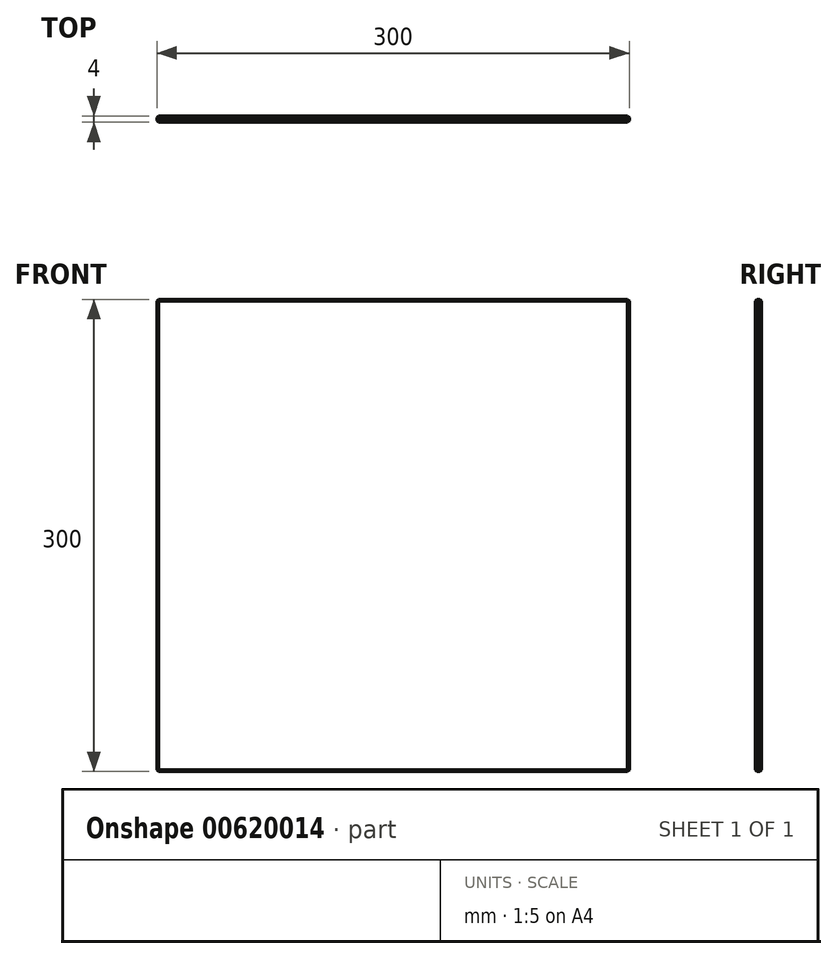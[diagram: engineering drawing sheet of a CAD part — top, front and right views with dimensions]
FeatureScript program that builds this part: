
annotation { "Feature Type Name" : "Feature", "Feature Type Description" : "" }
export const myFeature = defineFeature(function(context is Context, id is Id, definition is map)
    precondition{}
    {
        {
            var Q0;
            Q0=qCreatedBy(makeId("Front.planeOp"),FACE);
            var sketch = newSketch(context, id + "F0", { "sketchPlane" : qUnion([Q0])});
            skLineSegment(sketch, "E0.bottom", {"start": v(-262.15, 270.21) * mm, "end": v(37.85, 270.21) * mm});
            skLineSegment(sketch, "E0.top", {"start": v(-262.15, -29.79) * mm, "end": v(37.85, -29.79) * mm});
            skLineSegment(sketch, "E0.left", {"start": v(-262.15, 270.21) * mm, "end": v(-262.15, -29.79) * mm});
            skLineSegment(sketch, "E0.right", {"start": v(37.85, 270.21) * mm, "end": v(37.85, -29.79) * mm});
            skSolve(sketch);
        }
        {
            var Q0;
            Q0 = qSketchRegion(id + "F0", true);
            extrude(context, id + "F1", {"entities" : qUnion([Q0]), "depth" : 4 * mm, "offsetDistance" : 25 * mm});
        }
        {
            var Q0;
            Q0=makeQuery(id+"F1.opExtrude","SWEPT_EDGE",EDGE,{"disambiguationData":[OSD([sQuery(id+"F0.wireOp",EDGE,"E0.bottom"),sQuery(id+"F0.wireOp",EDGE,"E0.left")])]});
            var Q1;
            Q1=makeQuery(id+"F1.opExtrude","SWEPT_EDGE",EDGE,{"disambiguationData":[OSD([sQuery(id+"F0.wireOp",EDGE,"E0.bottom"),sQuery(id+"F0.wireOp",EDGE,"E0.right")])]});
            var Q2;
            Q2=makeQuery(id+"F1.opExtrude","SWEPT_EDGE",EDGE,{"disambiguationData":[OSD([sQuery(id+"F0.wireOp",EDGE,"E0.top"),sQuery(id+"F0.wireOp",EDGE,"E0.right")])]});
            var Q3;
            Q3=makeQuery(id+"F1.opExtrude","SWEPT_EDGE",EDGE,{"disambiguationData":[OSD([sQuery(id+"F0.wireOp",EDGE,"E0.top"),sQuery(id+"F0.wireOp",EDGE,"E0.left")])]});
            chamfer(context, id + "F2", {"entities" : qUnion([Q0, Q1, Q2, Q3]), "width" : 1 * mm, "tangentPropagation" : true});
        }
        {
            var Q0;
            Q0=makeQuery(id+"F1.opExtrude","CAP_EDGE",EDGE,{"disambiguationData":[OSD([sQuery(id+"F0.wireOp",EDGE,"E0.top")])],"isStart":false});
            var Q1;
            {var subQ0=sQuery(id+"F0.wireOp",EDGE,"E0.left");var subQ1=sQuery(id+"F0.wireOp",EDGE,"E0.top");Q1=makeQuery(id+"F2.opChamfer","BLEND_EDGE",EDGE,{"blendedFrom":[makeQuery(id+"F1.opExtrude","SWEPT_EDGE",EDGE,{"disambiguationData":[OSD([subQ1,subQ0])]}),makeQuery(id+"F1.opExtrude","CAP_FACE",FACE,{"disambiguationData":[OSD([sQuery(id+"F0.wireOp",EDGE,"E0.bottom"),subQ1,subQ0,sQuery(id+"F0.wireOp",EDGE,"E0.right")])],"isStart":false})],"blendedInto":[makeQuery(id+"F1.opExtrude","CAP_FACE",FACE,{"disambiguationData":[OSD([sQuery(id+"F0.wireOp",EDGE,"E0.bottom"),subQ1,subQ0,sQuery(id+"F0.wireOp",EDGE,"E0.right")])],"isStart":false})]});}
            var Q2;
            Q2=makeQuery(id+"F1.opExtrude","CAP_EDGE",EDGE,{"disambiguationData":[OSD([sQuery(id+"F0.wireOp",EDGE,"E0.left")])],"isStart":false});
            var Q3;
            {var subQ0=sQuery(id+"F0.wireOp",EDGE,"E0.right");var subQ1=sQuery(id+"F0.wireOp",EDGE,"E0.top");Q3=makeQuery(id+"F2.opChamfer","BLEND_EDGE",EDGE,{"blendedFrom":[makeQuery(id+"F1.opExtrude","SWEPT_EDGE",EDGE,{"disambiguationData":[OSD([subQ1,subQ0])]}),makeQuery(id+"F1.opExtrude","CAP_FACE",FACE,{"disambiguationData":[OSD([sQuery(id+"F0.wireOp",EDGE,"E0.bottom"),subQ1,sQuery(id+"F0.wireOp",EDGE,"E0.left"),subQ0])],"isStart":false})],"blendedInto":[makeQuery(id+"F1.opExtrude","CAP_FACE",FACE,{"disambiguationData":[OSD([sQuery(id+"F0.wireOp",EDGE,"E0.bottom"),subQ1,sQuery(id+"F0.wireOp",EDGE,"E0.left"),subQ0])],"isStart":false})]});}
            var Q4;
            Q4=makeQuery(id+"F1.opExtrude","CAP_EDGE",EDGE,{"disambiguationData":[OSD([sQuery(id+"F0.wireOp",EDGE,"E0.right")])],"isStart":false});
            var Q5;
            Q5=makeQuery(id+"F1.opExtrude","CAP_EDGE",EDGE,{"disambiguationData":[OSD([sQuery(id+"F0.wireOp",EDGE,"E0.right")])],"isStart":true});
            var Q6;
            {var subQ0=sQuery(id+"F0.wireOp",EDGE,"E0.right");var subQ1=sQuery(id+"F0.wireOp",EDGE,"E0.top");Q6=makeQuery(id+"F2.opChamfer","BLEND_EDGE",EDGE,{"blendedFrom":[makeQuery(id+"F1.opExtrude","SWEPT_EDGE",EDGE,{"disambiguationData":[OSD([subQ1,subQ0])]}),makeQuery(id+"F1.opExtrude","CAP_FACE",FACE,{"disambiguationData":[OSD([sQuery(id+"F0.wireOp",EDGE,"E0.bottom"),subQ1,sQuery(id+"F0.wireOp",EDGE,"E0.left"),subQ0])],"isStart":true})],"blendedInto":[makeQuery(id+"F1.opExtrude","CAP_FACE",FACE,{"disambiguationData":[OSD([sQuery(id+"F0.wireOp",EDGE,"E0.bottom"),subQ1,sQuery(id+"F0.wireOp",EDGE,"E0.left"),subQ0])],"isStart":true})]});}
            var Q7;
            Q7=makeQuery(id+"F1.opExtrude","CAP_EDGE",EDGE,{"disambiguationData":[OSD([sQuery(id+"F0.wireOp",EDGE,"E0.top")])],"isStart":true});
            var Q8;
            {var subQ0=sQuery(id+"F0.wireOp",EDGE,"E0.left");var subQ1=sQuery(id+"F0.wireOp",EDGE,"E0.top");Q8=makeQuery(id+"F2.opChamfer","BLEND_EDGE",EDGE,{"blendedFrom":[makeQuery(id+"F1.opExtrude","SWEPT_EDGE",EDGE,{"disambiguationData":[OSD([subQ1,subQ0])]}),makeQuery(id+"F1.opExtrude","CAP_FACE",FACE,{"disambiguationData":[OSD([sQuery(id+"F0.wireOp",EDGE,"E0.bottom"),subQ1,subQ0,sQuery(id+"F0.wireOp",EDGE,"E0.right")])],"isStart":true})],"blendedInto":[makeQuery(id+"F1.opExtrude","CAP_FACE",FACE,{"disambiguationData":[OSD([sQuery(id+"F0.wireOp",EDGE,"E0.bottom"),subQ1,subQ0,sQuery(id+"F0.wireOp",EDGE,"E0.right")])],"isStart":true})]});}
            var Q9;
            Q9=makeQuery(id+"F1.opExtrude","CAP_EDGE",EDGE,{"disambiguationData":[OSD([sQuery(id+"F0.wireOp",EDGE,"E0.left")])],"isStart":true});
            var Q10;
            {var subQ0=sQuery(id+"F0.wireOp",EDGE,"E0.left");var subQ1=sQuery(id+"F0.wireOp",EDGE,"E0.bottom");Q10=makeQuery(id+"F2.opChamfer","BLEND_EDGE",EDGE,{"blendedFrom":[makeQuery(id+"F1.opExtrude","SWEPT_EDGE",EDGE,{"disambiguationData":[OSD([subQ1,subQ0])]}),makeQuery(id+"F1.opExtrude","CAP_FACE",FACE,{"disambiguationData":[OSD([subQ1,sQuery(id+"F0.wireOp",EDGE,"E0.top"),subQ0,sQuery(id+"F0.wireOp",EDGE,"E0.right")])],"isStart":false})],"blendedInto":[makeQuery(id+"F1.opExtrude","CAP_FACE",FACE,{"disambiguationData":[OSD([subQ1,sQuery(id+"F0.wireOp",EDGE,"E0.top"),subQ0,sQuery(id+"F0.wireOp",EDGE,"E0.right")])],"isStart":false})]});}
            var Q11;
            {var subQ0=sQuery(id+"F0.wireOp",EDGE,"E0.left");var subQ1=sQuery(id+"F0.wireOp",EDGE,"E0.bottom");Q11=makeQuery(id+"F2.opChamfer","BLEND_EDGE",EDGE,{"blendedFrom":[makeQuery(id+"F1.opExtrude","SWEPT_EDGE",EDGE,{"disambiguationData":[OSD([subQ1,subQ0])]}),makeQuery(id+"F1.opExtrude","CAP_FACE",FACE,{"disambiguationData":[OSD([subQ1,sQuery(id+"F0.wireOp",EDGE,"E0.top"),subQ0,sQuery(id+"F0.wireOp",EDGE,"E0.right")])],"isStart":true})],"blendedInto":[makeQuery(id+"F1.opExtrude","CAP_FACE",FACE,{"disambiguationData":[OSD([subQ1,sQuery(id+"F0.wireOp",EDGE,"E0.top"),subQ0,sQuery(id+"F0.wireOp",EDGE,"E0.right")])],"isStart":true})]});}
            var Q12;
            Q12=makeQuery(id+"F1.opExtrude","CAP_EDGE",EDGE,{"disambiguationData":[OSD([sQuery(id+"F0.wireOp",EDGE,"E0.bottom")])],"isStart":true});
            var Q13;
            Q13=makeQuery(id+"F1.opExtrude","CAP_EDGE",EDGE,{"disambiguationData":[OSD([sQuery(id+"F0.wireOp",EDGE,"E0.bottom")])],"isStart":false});
            var Q14;
            {var subQ0=sQuery(id+"F0.wireOp",EDGE,"E0.right");var subQ1=sQuery(id+"F0.wireOp",EDGE,"E0.bottom");Q14=makeQuery(id+"F2.opChamfer","BLEND_EDGE",EDGE,{"blendedFrom":[makeQuery(id+"F1.opExtrude","SWEPT_EDGE",EDGE,{"disambiguationData":[OSD([subQ1,subQ0])]}),makeQuery(id+"F1.opExtrude","CAP_FACE",FACE,{"disambiguationData":[OSD([subQ1,sQuery(id+"F0.wireOp",EDGE,"E0.top"),sQuery(id+"F0.wireOp",EDGE,"E0.left"),subQ0])],"isStart":false})],"blendedInto":[makeQuery(id+"F1.opExtrude","CAP_FACE",FACE,{"disambiguationData":[OSD([subQ1,sQuery(id+"F0.wireOp",EDGE,"E0.top"),sQuery(id+"F0.wireOp",EDGE,"E0.left"),subQ0])],"isStart":false})]});}
            var Q15;
            {var subQ0=sQuery(id+"F0.wireOp",EDGE,"E0.right");var subQ1=sQuery(id+"F0.wireOp",EDGE,"E0.bottom");Q15=makeQuery(id+"F2.opChamfer","BLEND_EDGE",EDGE,{"blendedFrom":[makeQuery(id+"F1.opExtrude","SWEPT_EDGE",EDGE,{"disambiguationData":[OSD([subQ1,subQ0])]}),makeQuery(id+"F1.opExtrude","CAP_FACE",FACE,{"disambiguationData":[OSD([subQ1,sQuery(id+"F0.wireOp",EDGE,"E0.top"),sQuery(id+"F0.wireOp",EDGE,"E0.left"),subQ0])],"isStart":true})],"blendedInto":[makeQuery(id+"F1.opExtrude","CAP_FACE",FACE,{"disambiguationData":[OSD([subQ1,sQuery(id+"F0.wireOp",EDGE,"E0.top"),sQuery(id+"F0.wireOp",EDGE,"E0.left"),subQ0])],"isStart":true})]});}
            chamfer(context, id + "F3", {"entities" : qUnion([Q0, Q1, Q2, Q3, Q4, Q5, Q6, Q7, Q8, Q9, Q10, Q11, Q12, Q13, Q14, Q15]), "width" : 1 * mm, "tangentPropagation" : true});
        }
    });
